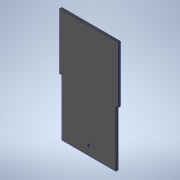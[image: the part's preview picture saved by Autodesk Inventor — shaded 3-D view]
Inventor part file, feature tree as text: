
AUTODESK INVENTOR PART (.ipt)
format: ipt  version: 2020 (Build 240168000, 168)  size: 122,880 bytes
history: native  units: mm
features: sketch x3, extrude x2, other x1, hole x1
ambient origin geometry x8: Origin, YZ Plane, XZ Plane, XY Plane, X Axis, Y Axis, Z Axis, Center Point
bodies: Body1 (feature_tree)
feature tree (7):
  other  "솔리드1"
  extrude  "돌출1"  Depth=250.0mm
  extrude  "돌출2"  Depth=10.0mm
  hole  "구멍1"  [1 undecoded]
  sketch  "스케치1"
  sketch  "스케치2"
  sketch  "스케치3"
note: 1 required parameter value undecoded (feature->parameter linkage not recoverable at this tier; creation-order binding heuristic only, values carry confidence <= 0.55)
